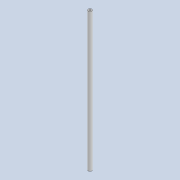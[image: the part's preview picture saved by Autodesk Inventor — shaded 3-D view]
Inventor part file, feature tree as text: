
AUTODESK INVENTOR PART (.ipt)
format: ipt  version: 2020 (Build 240168000, 168)  size: 71,680 bytes
history: native  units: mm
features: extrude x1, sketch x1
ambient origin geometry x8: Origin, YZ Plane, XZ Plane, XY Plane, X Axis, Y Axis, Z Axis, Center Point
bodies: Solid1 (feature_tree)
feature tree (2):
  extrude  "Extrusion1"  Depth=60.0mm
  sketch  "Sketch1"  dims[d0=0.8mm d1=1.6mm d2=60.0mm d3=0.0mm]
